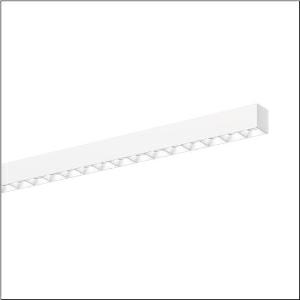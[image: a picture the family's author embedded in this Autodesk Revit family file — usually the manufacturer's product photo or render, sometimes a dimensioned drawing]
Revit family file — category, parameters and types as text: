
# Revit family: silica_r__21_51mx26db45wb_cce2
name_source: partatom
category: Lighting Fixtures
units: mm (PartAtom-declared; Revit-internal decimal feet)

## family parameters
Cut with Voids When Loaded = No
Host = Face
Light Source = No
Part Type = Normal
Room Calculation Point = No
Round Connector Dimension = Use Diameter
Shared = No

## types (1)
- --- (1 x LED, 5400 lm, 29.3 W, 4000K)
    Apparent Load = 29 VA
    CIE Flux Codes = 83 98 100 100 100
    Color Rendering = 80
    Color Temperature = 4000K
    Default Elevation = 1800 mm
    Description = Silica® 21, office luminaire, primary light control with darklight reflector, of PMMA, white, CAT 2 (L<= 3000cd/m²), light emission: direct distribution, primary light characteristic: symmetric, installation type: surface-mounted, LED, rated luminous flux: 5.400lm, luminous efficacy: 184lm/W, light colour: 840, colour temperature: 4000K, with terminal, 3+2-pole, max. 2.5mm², mains connection: 220..240V, AC, 50/60Hz, rated input power: 29.3W, luminaire housing, of aluminium, traffic white (RAL 9016), length: 1.504mm, width: 53mm, height: 53mm, protection rating (complete): IP20, insulation class (complete): insulation class I (protective earthing), certification: CE, permissible operating ambient temperature: 0..+35°C, standard: EN 50419, packaging unit: 1 piece
    Height = 0 mm  [stored 0 ft]
    Lamp = 1 x LED
    Lamp Light Flux = 5400 lm
    Lamp Power = 29.3 W
    Lamp count = 1
    Length = 1504 mm
    Luminous efficacy = 184 lm/W
    Manufacturer = Siteco
    ModVariant = No
    Model = 51MX26DB45WB
    Mounting Place = Ceiling
    Mounting Type = Recessed
    Number of Poles = 1
    OnlyDefault = Yes
    Power Factor = 1
    Product Name = Silica® 21
    Product group = office luminaire | ceiling recessed
    ProductGroupID = 401
    Protection Class = Protection class I
    Protection Degree = IP 20
    RLX_Detail_Level = 1
    RLX_Emergency_Light_Flux = 0 lm
    RLX_Emergency_Type = 0
    RLX_Emergency_Type_DB = No
    RlxData = <blob elided: 41949 chars, md5=fc9cece7>
    Socket = socket
    Standby Power = 0 W
    System Light Flux = 5400 lm
    System Power = 29 W
    Type Comments = factory setting: luminous flux: 100 % | dim-lin: 254 | 336 mA
    Type Image = l_1313597.jpg
    URL = http://relux.com
    VarID = @adj_073567
    Voltage = 0 V
    Weight = 0.00 kg
    Width = 53 mm

note: [stored X ft] marks values corroborated as IEEE doubles in the binary element streams (Revit-internal decimal feet)

## geometry (parser evidence)
native form markers: Blend x4, Sweep x10
no freeform markers — native parametric forms only
